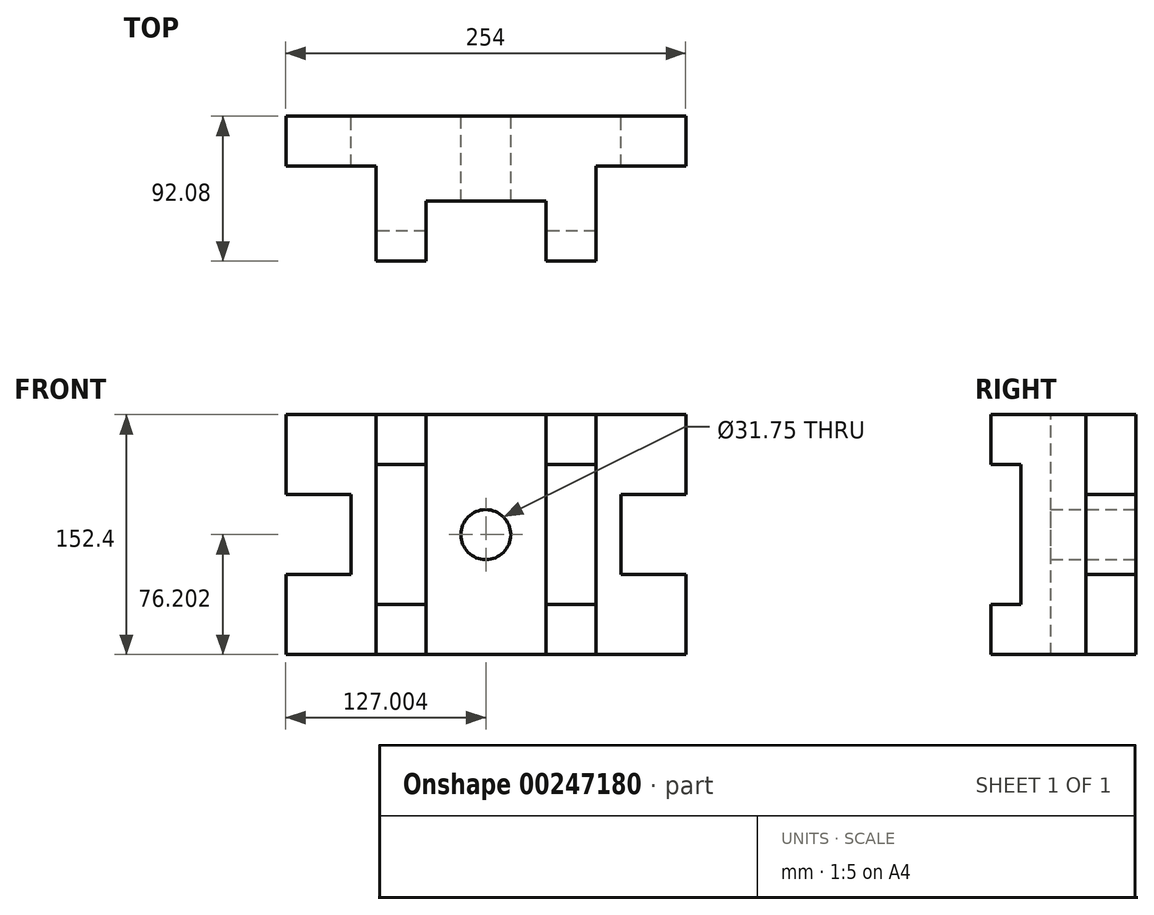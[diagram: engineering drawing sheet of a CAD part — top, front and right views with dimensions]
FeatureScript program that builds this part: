
annotation { "Feature Type Name" : "Feature", "Feature Type Description" : "" }
export const myFeature = defineFeature(function(context is Context, id is Id, definition is map)
    precondition{}
    {
        {
            var Q0;
            Q0=qCreatedBy(makeId("Front.planeOp"),FACE);
            var sketch = newSketch(context, id + "F0", { "sketchPlane" : qUnion([Q0])});
            skLineSegment(sketch, "E0.bottom", {"start": v(-111.29, 78.08) * mm, "end": v(142.71, 78.08) * mm});
            skLineSegment(sketch, "E0.top", {"start": v(-111.29, -74.32) * mm, "end": v(142.71, -74.32) * mm});
            skLineSegment(sketch, "E0.left", {"start": v(-111.29, 78.08) * mm, "end": v(-111.29, 27.28) * mm});
            skLineSegment(sketch, "E0.right", {"start": v(142.71, 78.08) * mm, "end": v(142.71, 27.28) * mm});
            skLineSegment(sketch, "E1", {"start": v(-54.14, 78.08) * mm, "end": v(-54.14, -74.32) * mm});
            skLineSegment(sketch, "E2", {"start": v(-22.39, 78.08) * mm, "end": v(-22.39, -74.32) * mm});
            skLineSegment(sketch, "E3", {"start": v(53.81, 78.08) * mm, "end": v(53.81, -74.32) * mm});
            skLineSegment(sketch, "E4", {"start": v(85.56, 78.08) * mm, "end": v(85.56, -74.32) * mm});
            skLineSegment(sketch, "E5", {"start": v(-54.14, 46.33) * mm, "end": v(-22.39, 46.33) * mm});
            skLineSegment(sketch, "E6", {"start": v(-54.14, -42.57) * mm, "end": v(-22.39, -42.57) * mm});
            skLineSegment(sketch, "E7.trimOffspring", {"start": v(53.81, 46.33) * mm, "end": v(85.56, 46.33) * mm});
            skLineSegment(sketch, "E8.trimOffspring", {"start": v(53.81, -42.57) * mm, "end": v(85.56, -42.57) * mm});
            skLineSegment(sketch, "E9", {"start": v(142.71, -23.52) * mm, "end": v(101.44, -23.52) * mm});
            skLineSegment(sketch, "E10", {"start": v(101.44, -23.52) * mm, "end": v(101.44, 27.28) * mm});
            skLineSegment(sketch, "E11", {"start": v(142.71, 27.28) * mm, "end": v(101.44, 27.28) * mm});
            skLineSegment(sketch, "E12", {"start": v(-111.29, 27.28) * mm, "end": v(-70.01, 27.28) * mm});
            skLineSegment(sketch, "E13", {"start": v(-70.01, 27.28) * mm, "end": v(-70.01, -23.52) * mm});
            skLineSegment(sketch, "E14", {"start": v(-70.01, -23.52) * mm, "end": v(-111.29, -23.52) * mm});
            skLineSegment(sketch, "E15.trimOffspring", {"start": v(-111.29, -23.52) * mm, "end": v(-111.29, -74.32) * mm});
            skLineSegment(sketch, "E16.trimOffspring", {"start": v(142.71, -23.52) * mm, "end": v(142.71, -74.32) * mm});
            skCircle(sketch, "E17", {"center": v(15.71, 1.88) * mm, "radius": 15.88 * mm});
            skSolve(sketch);
        }
        {
            var Q0;
            {var subQ7=sQuery(id+"F0.wireOp",EDGE,"E0.left");Q0=makeQuery(id+"F0.imprint","IMPRINT",FACE,{"disambiguationData":[TD([[makeQuery(id+"F0.imprint","IMPRINT",EDGE,{"derivedFrom":subQ7}),1.0]])]});}
            var Q1;
            {var subQ5=sQuery(id+"F0.wireOp",EDGE,"E5");Q1=makeQuery(id+"F0.imprint","IMPRINT",FACE,{"disambiguationData":[TD([[makeQuery(id+"F0.imprint","IMPRINT",EDGE,{"derivedFrom":subQ5}),1.0]])]});}
            var Q2;
            {var subQ0=sQuery(id+"F0.wireOp",EDGE,"E5");Q2=makeQuery(id+"F0.imprint","IMPRINT",FACE,{"disambiguationData":[TD([[makeQuery(id+"F0.imprint","IMPRINT",EDGE,{"derivedFrom":subQ0}),-1.0]])]});}
            var Q3;
            {var subQ5=sQuery(id+"F0.wireOp",EDGE,"E6");Q3=makeQuery(id+"F0.imprint","IMPRINT",FACE,{"disambiguationData":[TD([[makeQuery(id+"F0.imprint","IMPRINT",EDGE,{"derivedFrom":subQ5}),-1.0]])]});}
            var Q4;
            Q4=makeQuery(id+"F0.imprint","IMPRINT",FACE,{"disambiguationData":[TD([[makeQuery(id+"F0.imprint","IMPRINT",EDGE,{"derivedFrom":sQuery(id+"F0.wireOp",EDGE,"E17")}),-1.0]])]});
            var Q5;
            {var subQ0=sQuery(id+"F0.wireOp",EDGE,"E7.trimOffspring");Q5=makeQuery(id+"F0.imprint","IMPRINT",FACE,{"disambiguationData":[TD([[makeQuery(id+"F0.imprint","IMPRINT",EDGE,{"derivedFrom":subQ0}),-1.0]])]});}
            var Q6;
            {var subQ5=sQuery(id+"F0.wireOp",EDGE,"E8.trimOffspring");Q6=makeQuery(id+"F0.imprint","IMPRINT",FACE,{"disambiguationData":[TD([[makeQuery(id+"F0.imprint","IMPRINT",EDGE,{"derivedFrom":subQ5}),-1.0]])]});}
            var Q7;
            {var subQ0=sQuery(id+"F0.wireOp",EDGE,"E0.right");Q7=makeQuery(id+"F0.imprint","IMPRINT",FACE,{"disambiguationData":[TD([[makeQuery(id+"F0.imprint","IMPRINT",EDGE,{"derivedFrom":subQ0}),-1.0]])]});}
            var Q8;
            {var subQ5=sQuery(id+"F0.wireOp",EDGE,"E7.trimOffspring");Q8=makeQuery(id+"F0.imprint","IMPRINT",FACE,{"disambiguationData":[TD([[makeQuery(id+"F0.imprint","IMPRINT",EDGE,{"derivedFrom":subQ5}),1.0]])]});}
            extrude(context, id + "F1", {"entities" : qUnion([Q0, Q1, Q2, Q3, Q4, Q5, Q6, Q7, Q8]), "depth" : 31.75 * mm});
        }
        {
            var Q0;
            {var subQ0=sQuery(id+"F0.wireOp",EDGE,"E5");Q0=makeQuery(id+"F0.imprint","IMPRINT",FACE,{"disambiguationData":[TD([[makeQuery(id+"F0.imprint","IMPRINT",EDGE,{"derivedFrom":subQ0}),-1.0]])]});}
            var Q1;
            {var subQ5=sQuery(id+"F0.wireOp",EDGE,"E5");Q1=makeQuery(id+"F0.imprint","IMPRINT",FACE,{"disambiguationData":[TD([[makeQuery(id+"F0.imprint","IMPRINT",EDGE,{"derivedFrom":subQ5}),1.0]])]});}
            var Q2;
            {var subQ5=sQuery(id+"F0.wireOp",EDGE,"E6");Q2=makeQuery(id+"F0.imprint","IMPRINT",FACE,{"disambiguationData":[TD([[makeQuery(id+"F0.imprint","IMPRINT",EDGE,{"derivedFrom":subQ5}),-1.0]])]});}
            var Q3;
            Q3=makeQuery(id+"F0.imprint","IMPRINT",FACE,{"disambiguationData":[TD([[makeQuery(id+"F0.imprint","IMPRINT",EDGE,{"derivedFrom":sQuery(id+"F0.wireOp",EDGE,"E17")}),-1.0]])]});
            var Q4;
            {var subQ0=sQuery(id+"F0.wireOp",EDGE,"E7.trimOffspring");Q4=makeQuery(id+"F0.imprint","IMPRINT",FACE,{"disambiguationData":[TD([[makeQuery(id+"F0.imprint","IMPRINT",EDGE,{"derivedFrom":subQ0}),-1.0]])]});}
            var Q5;
            {var subQ5=sQuery(id+"F0.wireOp",EDGE,"E8.trimOffspring");Q5=makeQuery(id+"F0.imprint","IMPRINT",FACE,{"disambiguationData":[TD([[makeQuery(id+"F0.imprint","IMPRINT",EDGE,{"derivedFrom":subQ5}),-1.0]])]});}
            var Q6;
            {var subQ5=sQuery(id+"F0.wireOp",EDGE,"E7.trimOffspring");Q6=makeQuery(id+"F0.imprint","IMPRINT",FACE,{"disambiguationData":[TD([[makeQuery(id+"F0.imprint","IMPRINT",EDGE,{"derivedFrom":subQ5}),1.0]])]});}
            extrude(context, id + "F2", {"entities" : qUnion([Q0, Q1, Q2, Q3, Q4, Q5, Q6]), "operationType" : NewBodyOperationType.ADD, "depth" : 53.97 * mm});
        }
        {
            var Q0;
            {var subQ5=sQuery(id+"F0.wireOp",EDGE,"E5");Q0=makeQuery(id+"F0.imprint","IMPRINT",FACE,{"disambiguationData":[TD([[makeQuery(id+"F0.imprint","IMPRINT",EDGE,{"derivedFrom":subQ5}),1.0]])]});}
            var Q1;
            {var subQ0=sQuery(id+"F0.wireOp",EDGE,"E5");Q1=makeQuery(id+"F0.imprint","IMPRINT",FACE,{"disambiguationData":[TD([[makeQuery(id+"F0.imprint","IMPRINT",EDGE,{"derivedFrom":subQ0}),-1.0]])]});}
            var Q2;
            {var subQ5=sQuery(id+"F0.wireOp",EDGE,"E6");Q2=makeQuery(id+"F0.imprint","IMPRINT",FACE,{"disambiguationData":[TD([[makeQuery(id+"F0.imprint","IMPRINT",EDGE,{"derivedFrom":subQ5}),-1.0]])]});}
            var Q3;
            {var subQ5=sQuery(id+"F0.wireOp",EDGE,"E8.trimOffspring");Q3=makeQuery(id+"F0.imprint","IMPRINT",FACE,{"disambiguationData":[TD([[makeQuery(id+"F0.imprint","IMPRINT",EDGE,{"derivedFrom":subQ5}),-1.0]])]});}
            var Q4;
            {var subQ0=sQuery(id+"F0.wireOp",EDGE,"E7.trimOffspring");Q4=makeQuery(id+"F0.imprint","IMPRINT",FACE,{"disambiguationData":[TD([[makeQuery(id+"F0.imprint","IMPRINT",EDGE,{"derivedFrom":subQ0}),-1.0]])]});}
            var Q5;
            {var subQ5=sQuery(id+"F0.wireOp",EDGE,"E7.trimOffspring");Q5=makeQuery(id+"F0.imprint","IMPRINT",FACE,{"disambiguationData":[TD([[makeQuery(id+"F0.imprint","IMPRINT",EDGE,{"derivedFrom":subQ5}),1.0]])]});}
            extrude(context, id + "F3", {"entities" : qUnion([Q0, Q1, Q2, Q3, Q4, Q5]), "operationType" : NewBodyOperationType.ADD, "depth" : 73.02 * mm});
        }
        {
            var Q0;
            {var subQ5=sQuery(id+"F0.wireOp",EDGE,"E5");Q0=makeQuery(id+"F0.imprint","IMPRINT",FACE,{"disambiguationData":[TD([[makeQuery(id+"F0.imprint","IMPRINT",EDGE,{"derivedFrom":subQ5}),1.0]])]});}
            var Q1;
            {var subQ5=sQuery(id+"F0.wireOp",EDGE,"E6");Q1=makeQuery(id+"F0.imprint","IMPRINT",FACE,{"disambiguationData":[TD([[makeQuery(id+"F0.imprint","IMPRINT",EDGE,{"derivedFrom":subQ5}),-1.0]])]});}
            var Q2;
            {var subQ5=sQuery(id+"F0.wireOp",EDGE,"E7.trimOffspring");Q2=makeQuery(id+"F0.imprint","IMPRINT",FACE,{"disambiguationData":[TD([[makeQuery(id+"F0.imprint","IMPRINT",EDGE,{"derivedFrom":subQ5}),1.0]])]});}
            var Q3;
            {var subQ5=sQuery(id+"F0.wireOp",EDGE,"E8.trimOffspring");Q3=makeQuery(id+"F0.imprint","IMPRINT",FACE,{"disambiguationData":[TD([[makeQuery(id+"F0.imprint","IMPRINT",EDGE,{"derivedFrom":subQ5}),-1.0]])]});}
            extrude(context, id + "F4", {"entities" : qUnion([Q0, Q1, Q2, Q3]), "operationType" : NewBodyOperationType.ADD, "depth" : 92.07 * mm});
        }
    });
